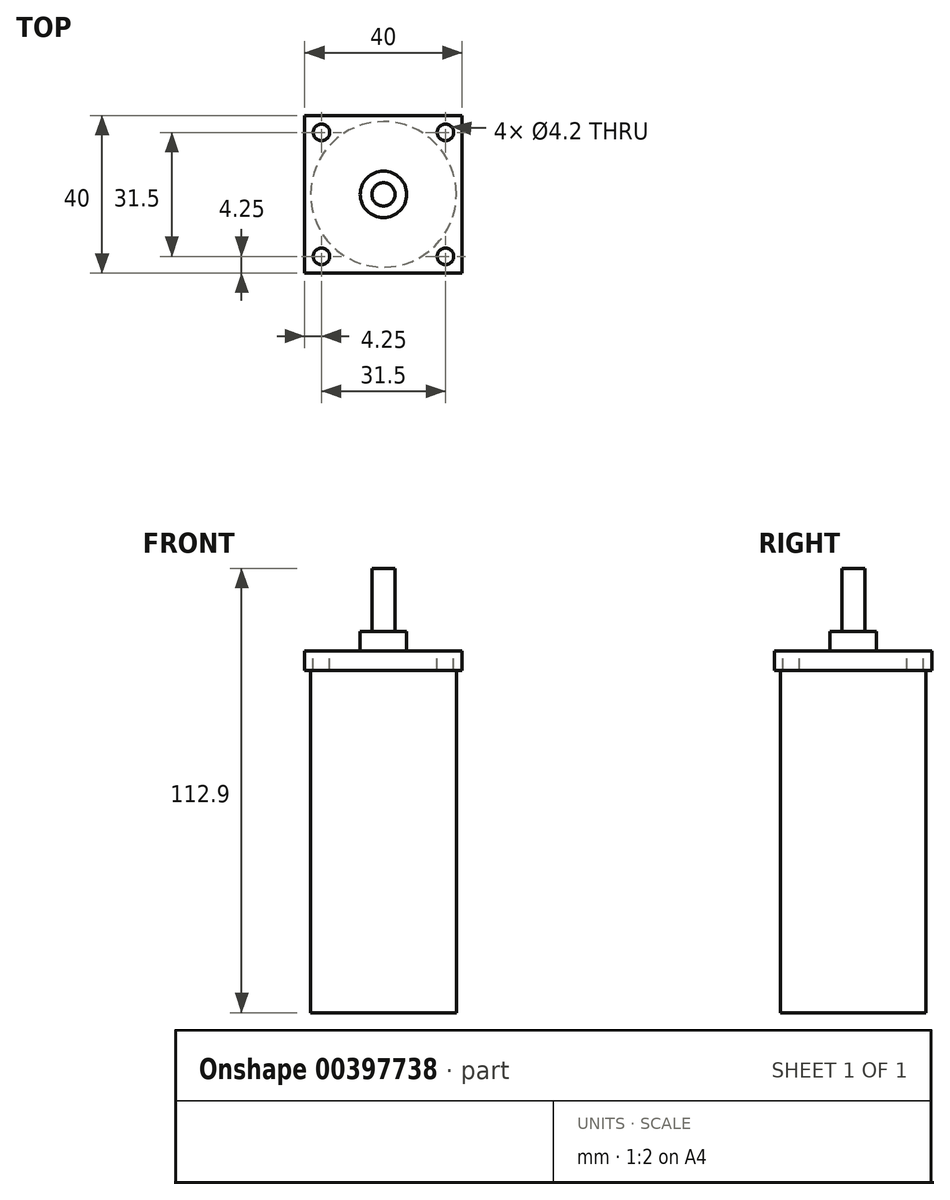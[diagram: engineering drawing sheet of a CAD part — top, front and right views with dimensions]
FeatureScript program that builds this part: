
annotation { "Feature Type Name" : "Feature", "Feature Type Description" : "" }
export const myFeature = defineFeature(function(context is Context, id is Id, definition is map)
    precondition{}
    {
        {
            var Q0;
            Q0=qCreatedBy(makeId("Top.planeOp"),FACE);
            var sketch = newSketch(context, id + "F0", { "sketchPlane" : qUnion([Q0])});
            skCircle(sketch, "E0", {"center": v(0, 0) * mm, "radius": 2.95 * mm});
            skCircle(sketch, "E1", {"center": v(0, 0) * mm, "radius": 5.9 * mm});
            skLineSegment(sketch, "E2.bottom", {"start": v(-20, 20) * mm, "end": v(20, 20) * mm});
            skLineSegment(sketch, "E2.top", {"start": v(-20, -20) * mm, "end": v(20, -20) * mm});
            skLineSegment(sketch, "E2.left", {"start": v(-20, 20) * mm, "end": v(-20, -20) * mm});
            skLineSegment(sketch, "E2.right", {"start": v(20, 20) * mm, "end": v(20, -20) * mm});
            skLineSegment(sketch, "E3", {"start": v(0, -20) * mm, "end": v(0, 0) * mm, "construction": true});
            skLineSegment(sketch, "E4", {"start": v(0, 0) * mm, "end": v(20, 0) * mm, "construction": true});
            skLineSegment(sketch, "E5.bottom", {"start": v(-15.75, 15.75) * mm, "end": v(15.75, 15.75) * mm});
            skLineSegment(sketch, "E5.top", {"start": v(-15.75, -15.75) * mm, "end": v(15.75, -15.75) * mm});
            skLineSegment(sketch, "E5.left", {"start": v(-15.75, 15.75) * mm, "end": v(-15.75, -15.75) * mm});
            skLineSegment(sketch, "E5.right", {"start": v(15.75, 15.75) * mm, "end": v(15.75, -15.75) * mm});
            skCircle(sketch, "E6", {"center": v(-15.75, 15.75) * mm, "radius": 2.1 * mm});
            skCircle(sketch, "E7", {"center": v(15.75, 15.75) * mm, "radius": 2.1 * mm});
            skCircle(sketch, "E8", {"center": v(15.75, -15.75) * mm, "radius": 2.1 * mm});
            skCircle(sketch, "E9", {"center": v(-15.75, -15.75) * mm, "radius": 2.1 * mm});
            skLineSegment(sketch, "E10", {"start": v(-15.75, 0) * mm, "end": v(-20, 0) * mm, "construction": true});
            skLineSegment(sketch, "E11", {"start": v(0, 20) * mm, "end": v(0, 15.75) * mm, "construction": true});
            skSolve(sketch);
        }
        {
            var Q0;
            Q0=makeQuery(id+"F0.imprint","IMPRINT",FACE,{"disambiguationData":[TD([[makeQuery(id+"F0.imprint","IMPRINT",EDGE,{"derivedFrom":sQuery(id+"F0.wireOp",EDGE,"E1")}),-1.0]])]});
            var Q1;
            Q1=makeQuery(id+"F0.imprint","IMPRINT",FACE,{"disambiguationData":[TD([[makeQuery(id+"F0.imprint","IMPRINT",EDGE,{"derivedFrom":sQuery(id+"F0.wireOp",EDGE,"E0")}),-1.0]])]});
            var Q2;
            Q2=makeQuery(id+"F0.imprint","IMPRINT",FACE,{"disambiguationData":[TD([[makeQuery(id+"F0.imprint","IMPRINT",EDGE,{"derivedFrom":sQuery(id+"F0.wireOp",EDGE,"E0")}),1.0]])]});
            var Q3;
            Q3=makeQuery(id+"F0.imprint","IMPRINT",FACE,{"disambiguationData":[TD([[makeQuery(id+"F0.imprint","IMPRINT",EDGE,{"derivedFrom":sQuery(id+"F0.wireOp",EDGE,"E2.bottom")}),-1.0]])]});
            extrude(context, id + "F1", {"entities" : qUnion([Q0, Q1, Q2, Q3]), "oppositeDirection" : true, "depth" : 4.9 * mm});
        }
        {
            var Q0;
            Q0=makeQuery(id+"F0.imprint","IMPRINT",FACE,{"disambiguationData":[TD([[makeQuery(id+"F0.imprint","IMPRINT",EDGE,{"derivedFrom":sQuery(id+"F0.wireOp",EDGE,"E0")}),1.0]])]});
            var Q1;
            Q1=sQuery(id+"F0.wireOp",EDGE,"E0");
            extrude(context, id + "F2", {"entities" : qUnion([Q0]), "operationType" : NewBodyOperationType.ADD, "surfaceEntities" : qUnion([Q1]), "depth" : 21 * mm});
        }
        {
            var Q0;
            Q0=makeQuery(id+"F0.imprint","IMPRINT",FACE,{"disambiguationData":[TD([[makeQuery(id+"F0.imprint","IMPRINT",EDGE,{"derivedFrom":sQuery(id+"F0.wireOp",EDGE,"E0")}),-1.0]])]});
            extrude(context, id + "F3", {"entities" : qUnion([Q0]), "operationType" : NewBodyOperationType.ADD, "depth" : 4.9 * mm});
        }
        {
            var Q0;
            Q0=makeQuery(id+"F1.opExtrude","CAP_FACE",FACE,{"disambiguationData":[OSD([sQuery(id+"F0.wireOp",EDGE,"E2.bottom"),sQuery(id+"F0.wireOp",EDGE,"E2.top"),sQuery(id+"F0.wireOp",EDGE,"E2.left"),sQuery(id+"F0.wireOp",EDGE,"E2.right"),sQuery(id+"F0.wireOp",EDGE,"E6"),sQuery(id+"F0.wireOp",EDGE,"E7"),sQuery(id+"F0.wireOp",EDGE,"E8"),sQuery(id+"F0.wireOp",EDGE,"E9")])],"isStart":false});
            var sketch = newSketch(context, id + "F4", { "sketchPlane" : qUnion([Q0])});
            skCircle(sketch, "E12", {"center": v(0, 0) * mm, "radius": 18.5 * mm});
            skSolve(sketch);
        }
        {
            var Q0;
            Q0=makeQuery(id+"F4.imprint","IMPRINT",FACE,{"disambiguationData":[TD([[makeQuery(id+"F4.imprint","IMPRINT",EDGE,{"derivedFrom":sQuery(id+"F4.wireOp",EDGE,"E12")}),1.0]])]});
            extrude(context, id + "F5", {"entities" : qUnion([Q0]), "operationType" : NewBodyOperationType.ADD, "depth" : 87 * mm});
        }
    });
